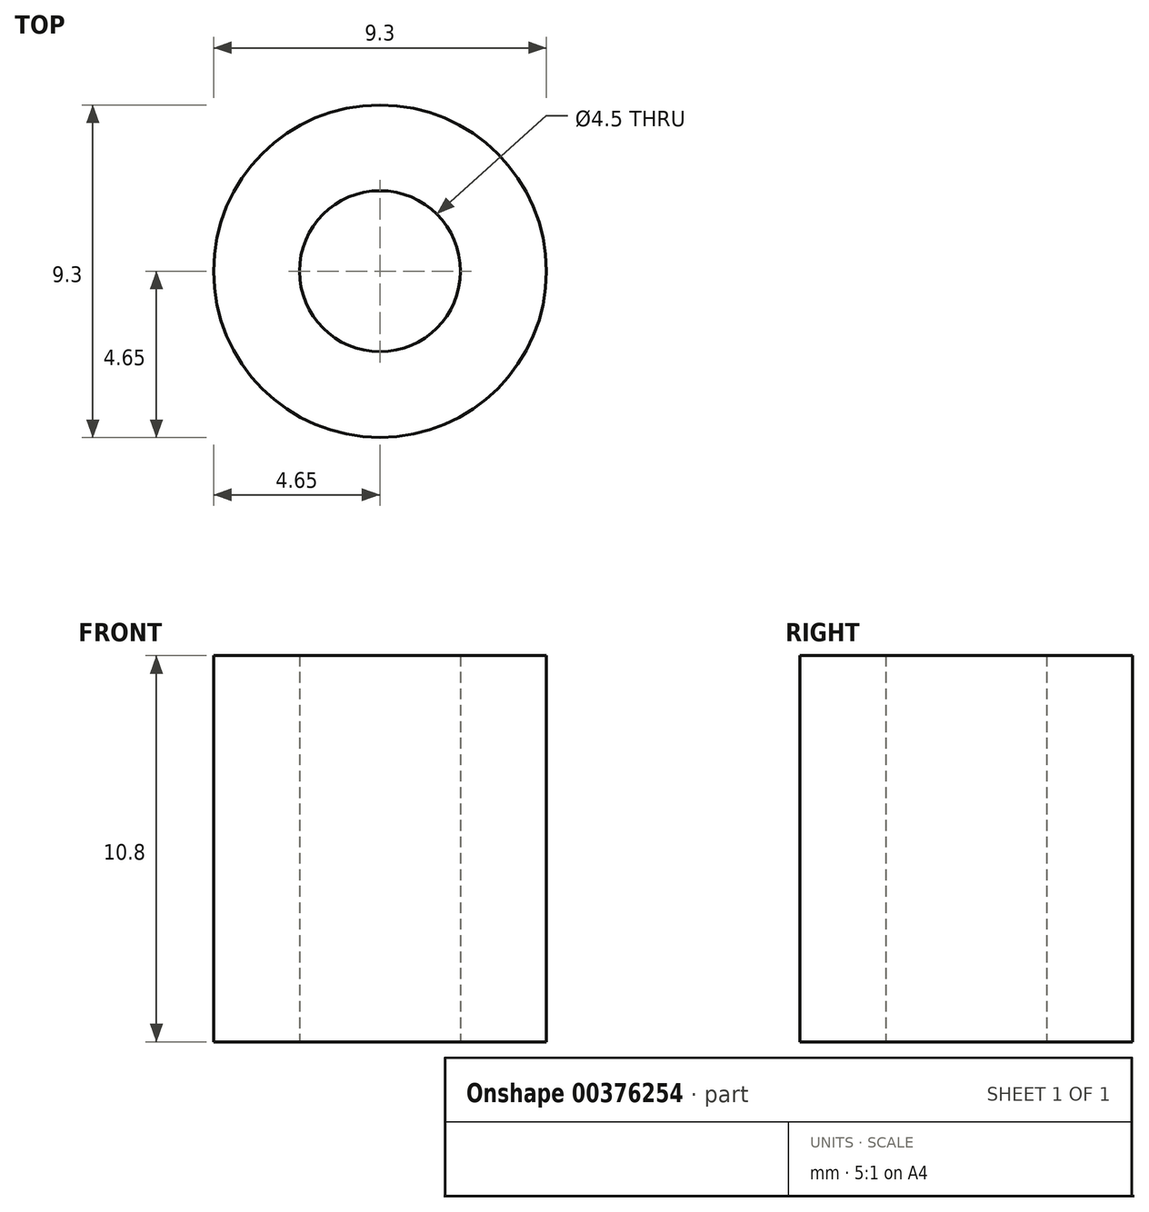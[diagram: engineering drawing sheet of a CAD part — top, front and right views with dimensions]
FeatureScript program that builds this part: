
annotation { "Feature Type Name" : "Feature", "Feature Type Description" : "" }
export const myFeature = defineFeature(function(context is Context, id is Id, definition is map)
    precondition{}
    {
        {
            var Q0;
            Q0=qCreatedBy(makeId("Top.planeOp"),FACE);
            var sketch = newSketch(context, id + "F0", { "sketchPlane" : qUnion([Q0])});
            skCircle(sketch, "E0", {"center": v(0, 0) * mm, "radius": 2.25 * mm});
            skCircle(sketch, "E1", {"center": v(0, 0) * mm, "radius": 4.65 * mm});
            skSolve(sketch);
        }
        {
            var Q0;
            Q0=makeQuery(id+"F0.imprint","IMPRINT",FACE,{"disambiguationData":[TD([[makeQuery(id+"F0.imprint","IMPRINT",EDGE,{"derivedFrom":sQuery(id+"F0.wireOp",EDGE,"E0")}),-1.0]])]});
            extrude(context, id + "F1", {"entities" : qUnion([Q0]), "depth" : 10.8 * mm});
        }
    });
